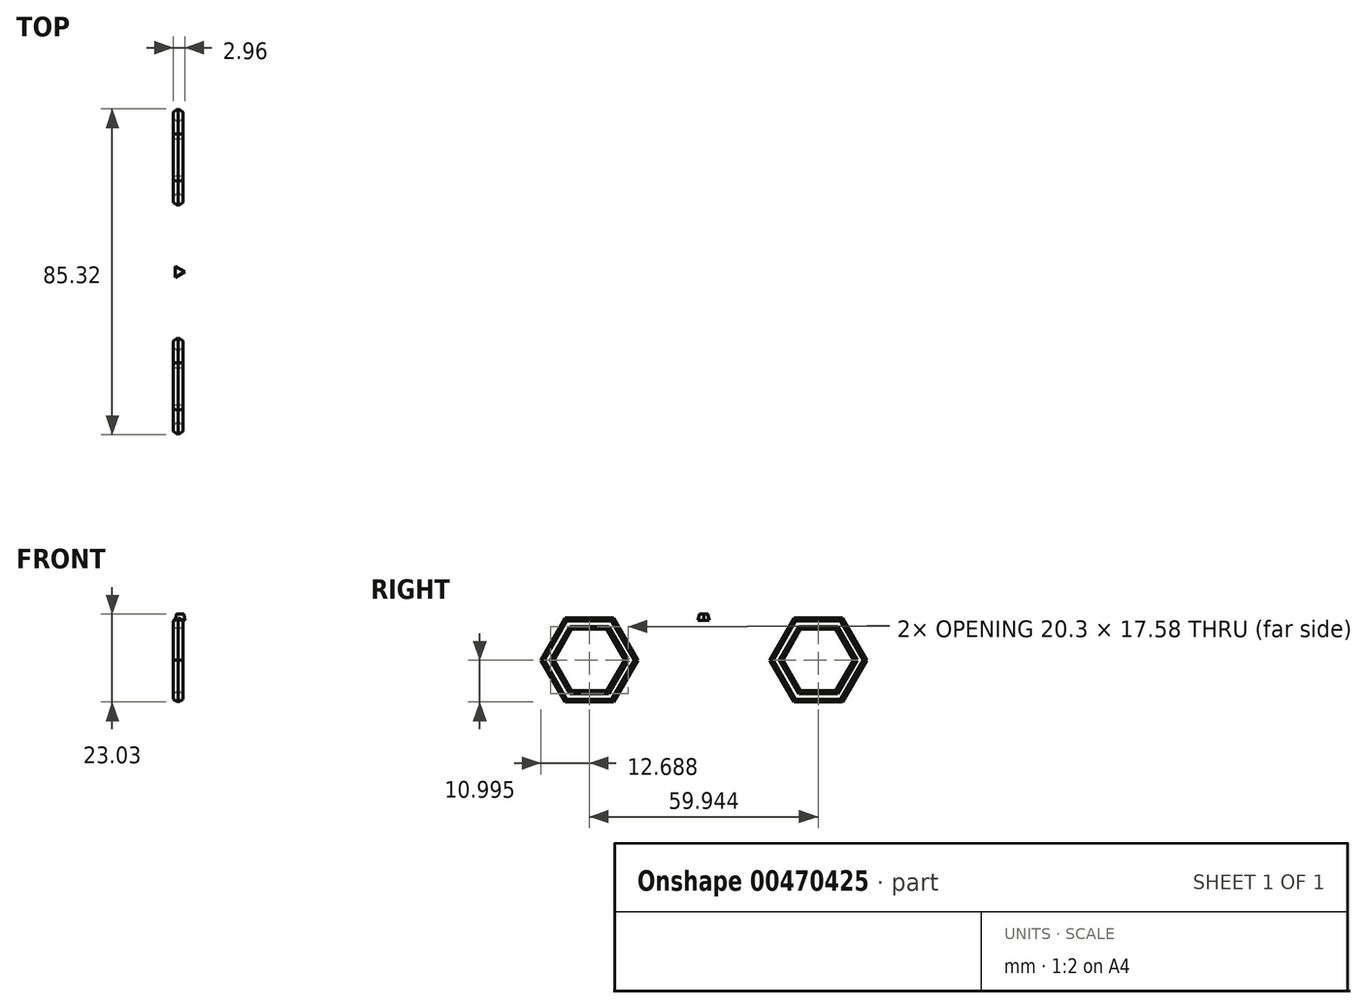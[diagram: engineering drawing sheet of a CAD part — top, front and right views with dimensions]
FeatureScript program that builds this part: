
annotation { "Feature Type Name" : "Feature", "Feature Type Description" : "" }
export const myFeature = defineFeature(function(context is Context, id is Id, definition is map)
    precondition{}
    {
        {
            var Q0;
            Q0=qCreatedBy(makeId("Front.planeOp"),FACE);
            var sketch = newSketch(context, id + "F0", { "sketchPlane" : qUnion([Q0])});
            skCircle(sketch, "E0.cCircle", {"center": v(0, 0) * mm, "radius": 1.27 * mm, "construction": true});
            skLineSegment(sketch, "E0.0", {"start": v(1.27, 0.73) * mm, "end": v(1.27, -0.73) * mm});
            skLineSegment(sketch, "E0.1", {"start": v(1.27, -0.73) * mm, "end": v(0, -1.47) * mm});
            skLineSegment(sketch, "E0.2", {"start": v(0, -1.47) * mm, "end": v(-1.27, -0.73) * mm});
            skLineSegment(sketch, "E0.3", {"start": v(-1.27, -0.73) * mm, "end": v(-1.27, 0.73) * mm});
            skLineSegment(sketch, "E0.4", {"start": v(-1.27, 0.73) * mm, "end": v(0, 1.47) * mm});
            skLineSegment(sketch, "E0.5", {"start": v(0, 1.47) * mm, "end": v(1.27, 0.73) * mm});
            skPoint(sketch, "E0.0.midPoint", {"position": v(1.27, 0) * mm});
            skSolve(sketch);
        }
        {
            var Q0;
            Q0=qCreatedBy(makeId("Right.planeOp"),FACE);
            var sketch = newSketch(context, id + "F1", { "sketchPlane" : qUnion([Q0])});
            skCircle(sketch, "E1.cCircle", {"center": v(0, 9.53) * mm, "radius": 11 * mm, "construction": true});
            skLineSegment(sketch, "E1.0", {"start": v(-5.5, 0) * mm, "end": v(-11, 9.52) * mm});
            skLineSegment(sketch, "E1.1", {"start": v(-11, 9.52) * mm, "end": v(-5.5, 19.05) * mm});
            skLineSegment(sketch, "E1.2", {"start": v(-5.5, 19.05) * mm, "end": v(5.5, 19.05) * mm});
            skLineSegment(sketch, "E1.3", {"start": v(5.5, 19.05) * mm, "end": v(11, 9.53) * mm});
            skLineSegment(sketch, "E1.4", {"start": v(11, 9.53) * mm, "end": v(5.5, 0) * mm});
            skLineSegment(sketch, "E1.5", {"start": v(5.5, 0) * mm, "end": v(-5.5, 0) * mm});
            skSolve(sketch);
        }
        {
            var Q0;
            Q0 = qSketchRegion(id + "F0", true);
            var Q1;
            Q1 = qConstructionFilter(qBodyType(qCreatedBy(id + "F1" ,EDGE), BodyType.WIRE), ConstructionObject.NO);
            sweep(context, id + "F2", {"profiles" : qUnion([Q0]), "path" : qUnion([Q1])});
        }
        {
            var Q0;
            Q0=qCreatedBy(makeId("Top.planeOp"),FACE);
            cPlane(context, id + "F3", {"entities" : qUnion([Q0]), "cplaneType" : CPlaneType.OFFSET, "offset" : 19.91 * mm, "width" : 152.4 * mm, "height" : 152.4 * mm});
        }
        {
            var Q0;
            Q0=qCreatedBy(id+"F3.planeOp",FACE);
            var sketch = newSketch(context, id + "F4", { "sketchPlane" : qUnion([Q0])});
            skCircle(sketch, "E2.cCircle", {"center": v(0, 0) * mm, "radius": 0.85 * mm, "construction": true});
            skLineSegment(sketch, "E2.0", {"start": v(-0.85, -1.47) * mm, "end": v(-0.85, 1.47) * mm});
            skLineSegment(sketch, "E2.1", {"start": v(-0.85, 1.47) * mm, "end": v(1.7, 0) * mm});
            skLineSegment(sketch, "E2.2", {"start": v(1.7, 0) * mm, "end": v(-0.85, -1.47) * mm});
            skPoint(sketch, "E2.0.midPoint", {"position": v(-0.85, 0) * mm});
            skSolve(sketch);
        }
        {
            var Q0;
            Q0=qCreatedBy(id+"F3.planeOp",FACE);
            cPlane(context, id + "F5", {"entities" : qUnion([Q0]), "cplaneType" : CPlaneType.OFFSET, "offset" : 1.65 * mm, "width" : 152.4 * mm, "height" : 152.4 * mm});
        }
        {
            var Q0;
            Q0=qCreatedBy(id+"F5.planeOp",FACE);
            var sketch = newSketch(context, id + "F6", { "sketchPlane" : qUnion([Q0])});
            skLineSegment(sketch, "E3", {"start": v(-0.46, 1.08) * mm, "end": v(-0.46, -1.08) * mm});
            skLineSegment(sketch, "E4", {"start": v(-0.46, -1.08) * mm, "end": v(1.41, 0) * mm});
            skLineSegment(sketch, "E5", {"start": v(1.41, 0) * mm, "end": v(-0.46, 1.08) * mm});
            skSolve(sketch);
        }
        {
            var Q0;
            Q0 = qSketchRegion(id + "F6", true);
            var Q1;
            Q1 = qSketchRegion(id + "F4", true);
            loft(context, id + "F7", {"sheetProfilesArray" : [{ "sheetProfileEntities" : qUnion([Q0]) }, { "sheetProfileEntities" : qUnion([Q1]) }]});
        }
        {
            var Q0;
            Q0=makeQuery(id+"F7.opLoft","CAP_FACE",FACE,{"disambiguationData":[OSD([makeQuery(id+"F6.imprint","IMPRINT",FACE,{"disambiguationData":[TD([[makeQuery(id+"F6.imprint","IMPRINT",EDGE,{"derivedFrom":sQuery(id+"F6.wireOp",EDGE,"E3")}),1.0]])]})])],"isStart":true});
            fillet(context, id + "F8", {"entities" : qUnion([Q0]), "radius" : 0.03 * mm, "tangentPropagation" : true, "allowEdgeOverflow" : false});
        }
        {
            var Q0;
            Q0=makeQuery(id+"F2.opSweep","SWEPT_BODY",BODY,{"disambiguationData":[OSD([sQuery(id+"F0.wireOp",EDGE,"E0.0"),sQuery(id+"F0.wireOp",EDGE,"E0.1"),sQuery(id+"F0.wireOp",EDGE,"E0.2"),sQuery(id+"F0.wireOp",EDGE,"E0.3"),sQuery(id+"F0.wireOp",EDGE,"E0.4"),sQuery(id+"F0.wireOp",EDGE,"E0.5"),sQuery(id+"F1.wireOp",EDGE,"E1.5")])]});
            var Q1;
            Q1=qCreatedBy(makeId("Front.planeOp"),FACE);
            transform(context, id + "F9", {"entities" : qUnion([Q0]), "transformType" : TransformType.TRANSLATION_DISTANCE, "transformDirection" : qUnion([Q1]), "distance" : 29.97 * mm, "makeCopy" : false});
        }
        {
            var Q0;
            Q0=makeQuery(id+"F2.opSweep","SWEPT_BODY",BODY,{"disambiguationData":[OSD([sQuery(id+"F0.wireOp",EDGE,"E0.0"),sQuery(id+"F0.wireOp",EDGE,"E0.1"),sQuery(id+"F0.wireOp",EDGE,"E0.2"),sQuery(id+"F0.wireOp",EDGE,"E0.3"),sQuery(id+"F0.wireOp",EDGE,"E0.4"),sQuery(id+"F0.wireOp",EDGE,"E0.5"),sQuery(id+"F1.wireOp",EDGE,"E1.5")])]});
            var Q1;
            Q1=qCreatedBy(makeId("Front.planeOp"),FACE);
            mirror(context, id + "F10", {"entities" : qUnion([Q0]), "mirrorPlane" : qUnion([Q1])});
        }
    });
